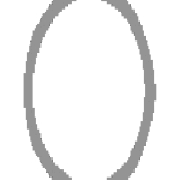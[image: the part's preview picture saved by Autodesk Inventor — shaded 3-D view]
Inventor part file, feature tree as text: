
AUTODESK INVENTOR PART (.ipt)
format: ipt  version: 2021 (Build 250183000, 183)  size: 109,568 bytes
history: native  units: in
note: dims shown in document units (in); Inventor stores cm internally (conversion verified against a paired STEP export)
features: other x4, sketch x3, plane x1
ambient origin geometry x8: Origin, YZ Plane, XZ Plane, XY Plane, X Axis, Y Axis, Z Axis, Center Point
bodies: Solid1 (feature_tree), Body (feature_tree)
feature tree (8):
  other  "Driven Length"
  other  "Frame Generator"
  other  "Start Plane"
  other  "End Plane"
  sketch  "Sketch"  dims[d2=12.431in d4=-0.0in d5=12.431in d6=0.12in d7=0.0in d8=90.0deg d9=12.431in]
  sketch  "Sketch2"  dims[d0=1.0in]
  plane  "Work Plane3"
  sketch  "Sketch3"  dims[d1=0.065in]
